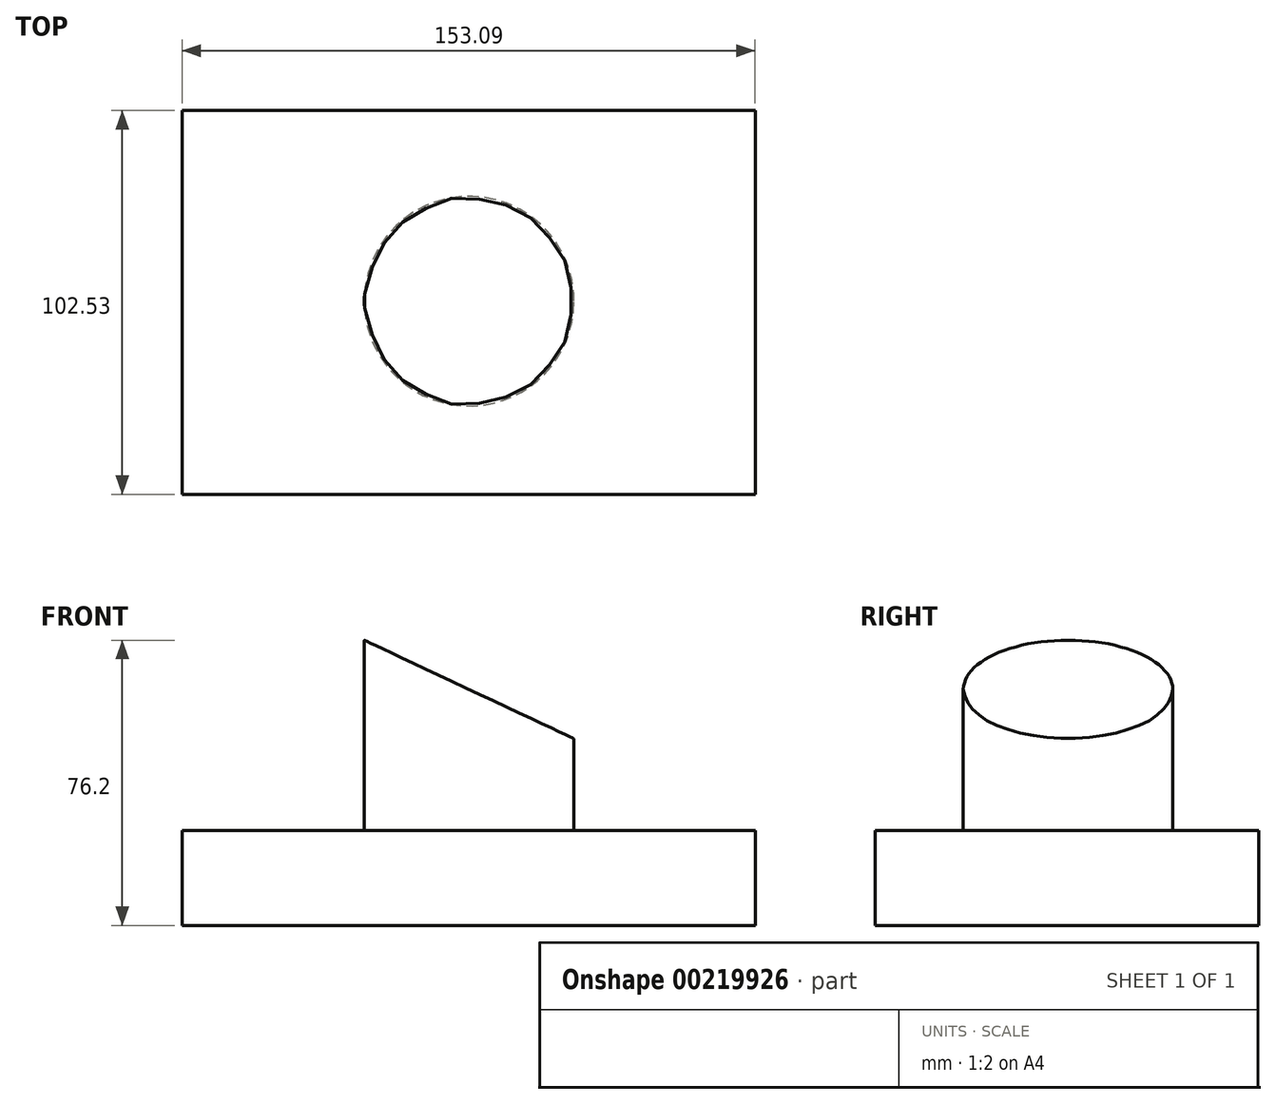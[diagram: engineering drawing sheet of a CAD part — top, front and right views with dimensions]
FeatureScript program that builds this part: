
annotation { "Feature Type Name" : "Feature", "Feature Type Description" : "" }
export const myFeature = defineFeature(function(context is Context, id is Id, definition is map)
    precondition{}
    {
        {
            var Q0;
            Q0=qCreatedBy(makeId("Top.planeOp"),FACE);
            var sketch = newSketch(context, id + "F0", { "sketchPlane" : qUnion([Q0])});
            skLineSegment(sketch, "E0.bottom", {"start": v(-76.66, 50.92) * mm, "end": v(76.43, 50.92) * mm});
            skLineSegment(sketch, "E0.top", {"start": v(-76.66, -51.6) * mm, "end": v(76.43, -51.6) * mm});
            skLineSegment(sketch, "E0.left", {"start": v(-76.66, 50.92) * mm, "end": v(-76.66, -51.6) * mm});
            skLineSegment(sketch, "E0.right", {"start": v(76.43, 50.92) * mm, "end": v(76.43, -51.6) * mm});
            skSolve(sketch);
        }
        {
            var Q0;
            Q0=makeQuery(id+"F0.imprint","IMPRINT",FACE,{"disambiguationData":[TD([[makeQuery(id+"F0.imprint","IMPRINT",EDGE,{"derivedFrom":sQuery(id+"F0.wireOp",EDGE,"E0.bottom")}),-1.0]])]});
            var Q1;
            Q1 = qSketchRegion(id + "F2", true);
            extrude(context, id + "F1", {"entities" : qUnion([Q0, Q1]), "depth" : 25.4 * mm});
        }
        {
            var Q0;
            Q0=makeQuery(id+"F1.opExtrude","CAP_FACE",FACE,{"disambiguationData":[OSD([sQuery(id+"F0.wireOp",EDGE,"E0.bottom"),sQuery(id+"F0.wireOp",EDGE,"E0.top"),sQuery(id+"F0.wireOp",EDGE,"E0.left"),sQuery(id+"F0.wireOp",EDGE,"E0.right")])],"isStart":false});
            var sketch = newSketch(context, id + "F2", { "sketchPlane" : qUnion([Q0])});
            skCircle(sketch, "E1", {"center": v(0, 0) * mm, "radius": 28 * mm});
            skSolve(sketch);
        }
        {
            var Q0;
            Q0=makeQuery(id+"F2.imprint","IMPRINT",FACE,{"disambiguationData":[TD([[makeQuery(id+"F2.imprint","IMPRINT",EDGE,{"derivedFrom":sQuery(id+"F2.wireOp",EDGE,"E1")}),1.0]])]});
            extrude(context, id + "F3", {"entities" : qUnion([Q0]), "operationType" : NewBodyOperationType.ADD, "depth" : 50.8 * mm});
        }
        {
            var Q0;
            Q0=makeQuery(id+"F1.opExtrude","SWEPT_FACE",FACE,{"disambiguationData":[OSD([sQuery(id+"F0.wireOp",EDGE,"E0.top")])]});
            var sketch = newSketch(context, id + "F4", { "sketchPlane" : qUnion([Q0])});
            skLineSegment(sketch, "E2.right", {"start": v(29.27, 77.58) * mm, "end": v(29.1, 49.39) * mm});
            skLineSegment(sketch, "E3", {"start": v(-30.87, 77.58) * mm, "end": v(29.1, 49.39) * mm});
            skLineSegment(sketch, "E4", {"start": v(-30.87, 77.58) * mm, "end": v(29.28, 77.58) * mm});
            skPoint(sketch, "E5.orphan", {"position": v(29.28, 78.74) * mm});
            skSolve(sketch);
        }
        {
            var Q0;
            Q0 = qSketchRegion(id + "F4", true);
            extrude(context, id + "F5", {"entities" : qUnion([Q0]), "operationType" : NewBodyOperationType.REMOVE, "oppositeDirection" : true, "depth" : 121.4 * mm});
        }
    });
